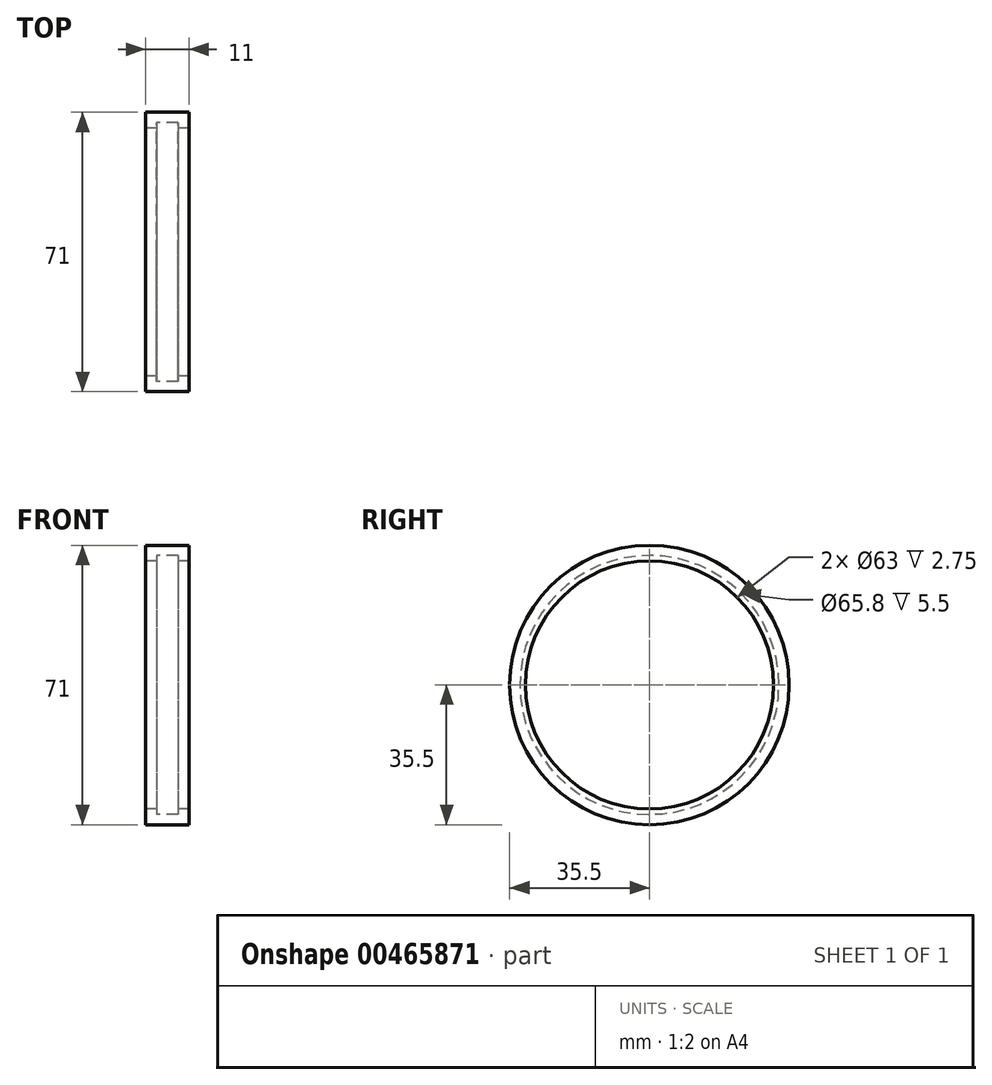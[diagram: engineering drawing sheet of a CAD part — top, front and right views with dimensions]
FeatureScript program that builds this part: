
annotation { "Feature Type Name" : "Feature", "Feature Type Description" : "" }
export const myFeature = defineFeature(function(context is Context, id is Id, definition is map)
    precondition{}
    {
        {
            var Q0;
            Q0=qCreatedBy(makeId("Front.planeOp"),FACE);
            var sketch = newSketch(context, id + "F0", { "sketchPlane" : qUnion([Q0])});
            skLineSegment(sketch, "E0", {"start": v(-5.5, 35.5) * mm, "end": v(-5.5, 31.5) * mm});
            skLineSegment(sketch, "E1", {"start": v(-5.5, 31.5) * mm, "end": v(-2.75, 31.5) * mm});
            skLineSegment(sketch, "E2", {"start": v(-2.75, 31.5) * mm, "end": v(-2.75, 32.9) * mm});
            skLineSegment(sketch, "E3", {"start": v(-2.75, 32.9) * mm, "end": v(2.75, 32.9) * mm});
            skLineSegment(sketch, "E4", {"start": v(2.75, 32.9) * mm, "end": v(2.75, 31.5) * mm});
            skLineSegment(sketch, "E5", {"start": v(2.75, 31.5) * mm, "end": v(5.5, 31.5) * mm});
            skLineSegment(sketch, "E6", {"start": v(5.5, 31.5) * mm, "end": v(5.5, 35.5) * mm});
            skLineSegment(sketch, "E7", {"start": v(5.5, 35.5) * mm, "end": v(-5.5, 35.5) * mm});
            skLineSegment(sketch, "E8", {"start": v(-7.18, 0) * mm, "end": v(4.77, 0) * mm, "construction": true});
            skSolve(sketch);
        }
        {
            var Q0;
            Q0=makeQuery(id+"F0.imprint","IMPRINT",FACE,{"disambiguationData":[TD([[makeQuery(id+"F0.imprint","IMPRINT",EDGE,{"derivedFrom":sQuery(id+"F0.wireOp",EDGE,"E0")}),1.0]])]});
            var Q1;
            Q1=sQuery(id+"F0.wireOp",EDGE,"E8");
            revolve(context, id + "F1", {"entities" : qUnion([Q0]), "axis" : qUnion([Q1]), "revolveType" : RevolveType.FULL});
        }
    });
